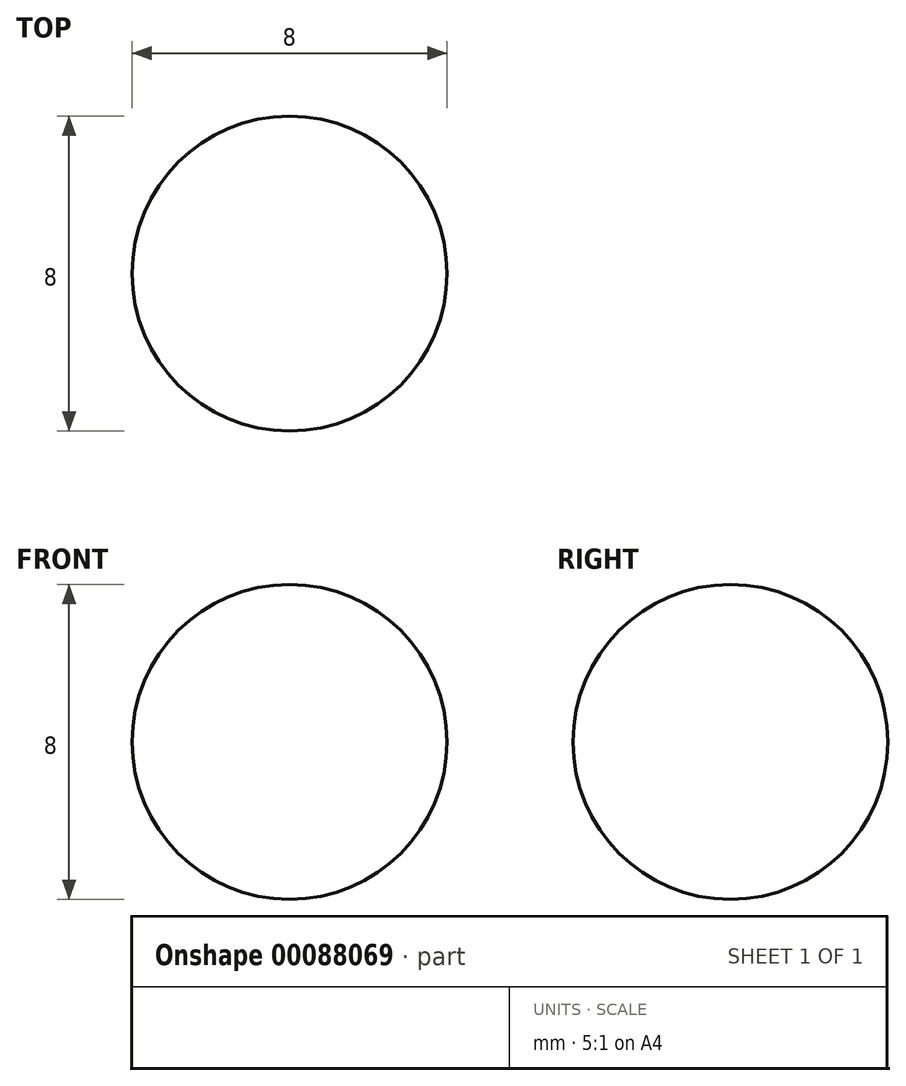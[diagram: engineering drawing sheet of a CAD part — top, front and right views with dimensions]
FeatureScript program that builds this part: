
annotation { "Feature Type Name" : "Feature", "Feature Type Description" : "" }
export const myFeature = defineFeature(function(context is Context, id is Id, definition is map)
    precondition{}
    {
        {
            var Q0;
            Q0=qCreatedBy(makeId("Front.planeOp"),FACE);
            var sketch = newSketch(context, id + "F0", { "sketchPlane" : qUnion([Q0])});
            skCircle(sketch, "E0", {"center": v(0, 0) * mm, "radius": 4 * mm});
            skLineSegment(sketch, "E1", {"start": v(0, 4) * mm, "end": v(0, -4) * mm});
            skSolve(sketch);
        }
        {
            var Q0;
            {var subQ0=sQuery(id+"F0.wireOp",EDGE,"E1");Q0=makeQuery(id+"F0.imprint","IMPRINT",FACE,{"disambiguationData":[TD([[makeQuery(id+"F0.imprint","IMPRINT",EDGE,{"derivedFrom":subQ0}),-1.0]])]});}
            var Q1;
            Q1=sQuery(id+"F0.wireOp",EDGE,"E1");
            revolve(context, id + "F1", {"entities" : qUnion([Q0]), "axis" : qUnion([Q1]), "revolveType" : RevolveType.FULL});
        }
    });
